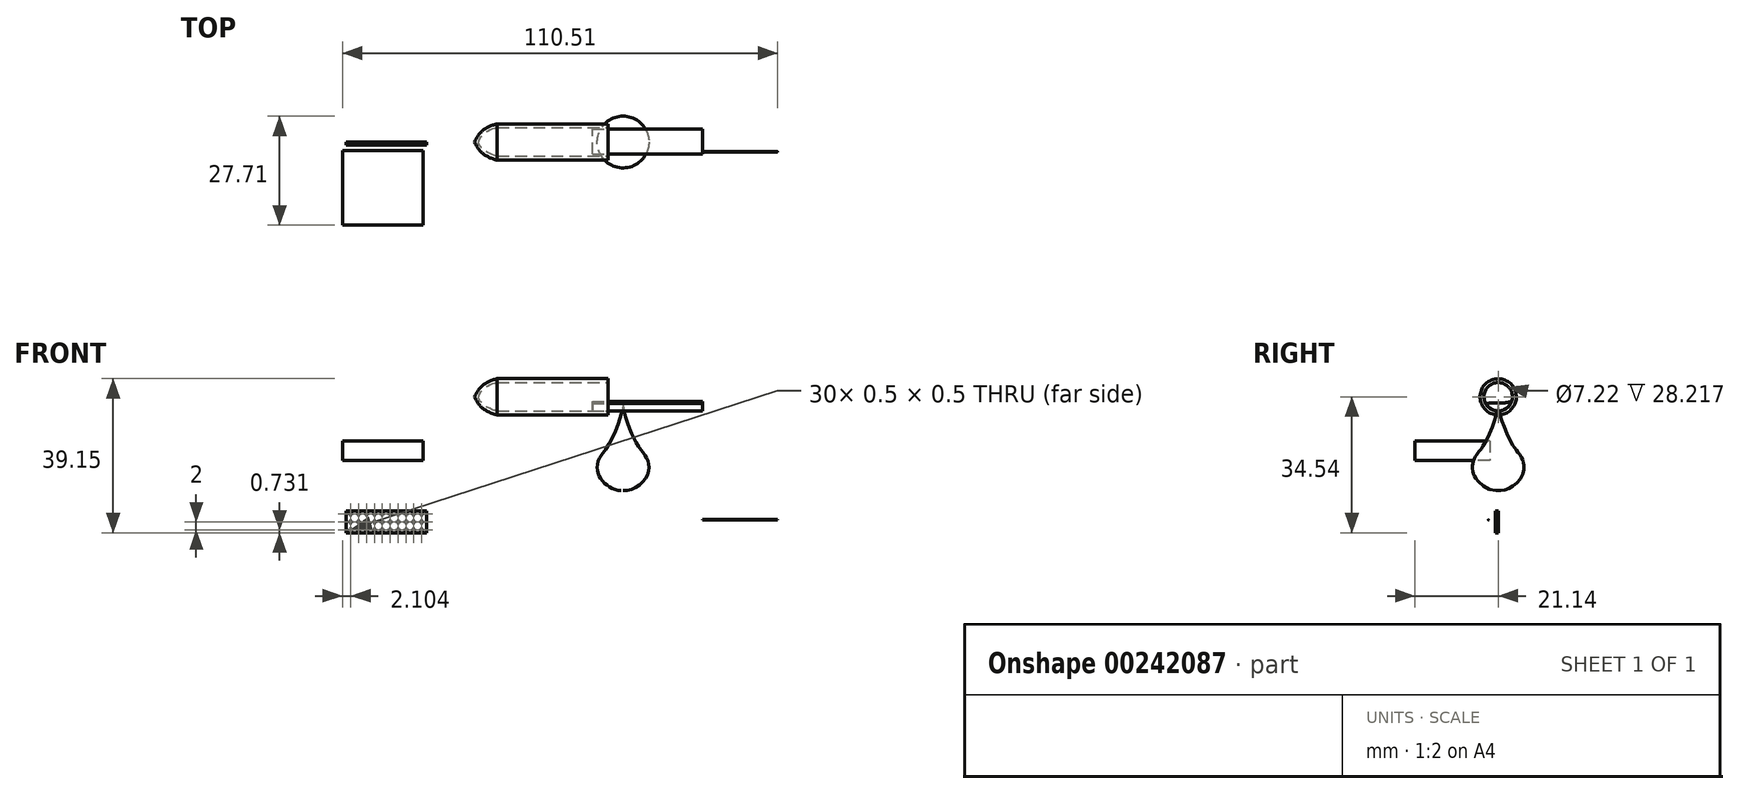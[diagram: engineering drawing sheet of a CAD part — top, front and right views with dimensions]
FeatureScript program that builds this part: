
annotation { "Feature Type Name" : "Feature", "Feature Type Description" : "" }
export const myFeature = defineFeature(function(context is Context, id is Id, definition is map)
    precondition{}
    {
        {
            var Q0;
            Q0=qCreatedBy(makeId("Front.planeOp"),FACE);
            var sketch = newSketch(context, id + "F0", { "sketchPlane" : qUnion([Q0])});
            skLineSegment(sketch, "E0.bottom", {"start": v(-89.66, -13.35) * mm, "end": v(-89.16, -13.35) * mm});
            skLineSegment(sketch, "E0.top", {"start": v(-89.66, -13.85) * mm, "end": v(-89.16, -13.85) * mm});
            skLineSegment(sketch, "E0.left", {"start": v(-89.66, -13.35) * mm, "end": v(-89.66, -13.85) * mm});
            skLineSegment(sketch, "E0.right", {"start": v(-89.16, -13.35) * mm, "end": v(-89.16, -13.85) * mm});
            skLineSegment(sketch, "E1.2.0.0", {"start": v(-87.66, -13.35) * mm, "end": v(-87.16, -13.35) * mm});
            skLineSegment(sketch, "E1.2.0.1", {"start": v(-87.16, -13.35) * mm, "end": v(-87.16, -13.85) * mm});
            skLineSegment(sketch, "E1.2.0.2", {"start": v(-87.66, -13.85) * mm, "end": v(-87.16, -13.85) * mm});
            skLineSegment(sketch, "E1.2.0.3", {"start": v(-87.66, -13.35) * mm, "end": v(-87.66, -13.85) * mm});
            skLineSegment(sketch, "E1.4.0.0", {"start": v(-85.66, -13.35) * mm, "end": v(-85.16, -13.35) * mm});
            skLineSegment(sketch, "E1.4.0.1", {"start": v(-85.16, -13.35) * mm, "end": v(-85.16, -13.85) * mm});
            skLineSegment(sketch, "E1.4.0.2", {"start": v(-85.66, -13.85) * mm, "end": v(-85.16, -13.85) * mm});
            skLineSegment(sketch, "E1.4.0.3", {"start": v(-85.66, -13.35) * mm, "end": v(-85.66, -13.85) * mm});
            skLineSegment(sketch, "E1.6.0.0", {"start": v(-83.66, -13.35) * mm, "end": v(-83.16, -13.35) * mm});
            skLineSegment(sketch, "E1.6.0.1", {"start": v(-83.16, -13.35) * mm, "end": v(-83.16, -13.85) * mm});
            skLineSegment(sketch, "E1.6.0.2", {"start": v(-83.66, -13.85) * mm, "end": v(-83.16, -13.85) * mm});
            skLineSegment(sketch, "E1.6.0.3", {"start": v(-83.66, -13.35) * mm, "end": v(-83.66, -13.85) * mm});
            skLineSegment(sketch, "E1.8.0.0", {"start": v(-81.66, -13.35) * mm, "end": v(-81.16, -13.35) * mm});
            skLineSegment(sketch, "E1.8.0.1", {"start": v(-81.16, -13.35) * mm, "end": v(-81.16, -13.85) * mm});
            skLineSegment(sketch, "E1.8.0.2", {"start": v(-81.66, -13.85) * mm, "end": v(-81.16, -13.85) * mm});
            skLineSegment(sketch, "E1.8.0.3", {"start": v(-81.66, -13.35) * mm, "end": v(-81.66, -13.85) * mm});
            skLineSegment(sketch, "E1.10.0.0", {"start": v(-79.66, -13.35) * mm, "end": v(-79.16, -13.35) * mm});
            skLineSegment(sketch, "E1.10.0.1", {"start": v(-79.16, -13.35) * mm, "end": v(-79.16, -13.85) * mm});
            skLineSegment(sketch, "E1.10.0.2", {"start": v(-79.66, -13.85) * mm, "end": v(-79.16, -13.85) * mm});
            skLineSegment(sketch, "E1.10.0.3", {"start": v(-79.66, -13.35) * mm, "end": v(-79.66, -13.85) * mm});
            skLineSegment(sketch, "E1.12.0.0", {"start": v(-77.66, -13.35) * mm, "end": v(-77.16, -13.35) * mm});
            skLineSegment(sketch, "E1.12.0.1", {"start": v(-77.16, -13.35) * mm, "end": v(-77.16, -13.85) * mm});
            skLineSegment(sketch, "E1.12.0.2", {"start": v(-77.66, -13.85) * mm, "end": v(-77.16, -13.85) * mm});
            skLineSegment(sketch, "E1.12.0.3", {"start": v(-77.66, -13.35) * mm, "end": v(-77.66, -13.85) * mm});
            skLineSegment(sketch, "E1.14.0.0", {"start": v(-75.66, -13.35) * mm, "end": v(-75.16, -13.35) * mm});
            skLineSegment(sketch, "E1.14.0.1", {"start": v(-75.16, -13.35) * mm, "end": v(-75.16, -13.85) * mm});
            skLineSegment(sketch, "E1.14.0.2", {"start": v(-75.66, -13.85) * mm, "end": v(-75.16, -13.85) * mm});
            skLineSegment(sketch, "E1.14.0.3", {"start": v(-75.66, -13.35) * mm, "end": v(-75.66, -13.85) * mm});
            skLineSegment(sketch, "E1.16.0.0", {"start": v(-73.66, -13.35) * mm, "end": v(-73.16, -13.35) * mm});
            skLineSegment(sketch, "E1.16.0.1", {"start": v(-73.16, -13.35) * mm, "end": v(-73.16, -13.85) * mm});
            skLineSegment(sketch, "E1.16.0.2", {"start": v(-73.66, -13.85) * mm, "end": v(-73.16, -13.85) * mm});
            skLineSegment(sketch, "E1.16.0.3", {"start": v(-73.66, -13.35) * mm, "end": v(-73.66, -13.85) * mm});
            skLineSegment(sketch, "E1.18.0.0", {"start": v(-71.66, -13.35) * mm, "end": v(-71.16, -13.35) * mm});
            skLineSegment(sketch, "E1.18.0.1", {"start": v(-71.16, -13.35) * mm, "end": v(-71.16, -13.85) * mm});
            skLineSegment(sketch, "E1.18.0.2", {"start": v(-71.66, -13.85) * mm, "end": v(-71.16, -13.85) * mm});
            skLineSegment(sketch, "E1.18.0.3", {"start": v(-71.66, -13.35) * mm, "end": v(-71.66, -13.85) * mm});
            skLineSegment(sketch, "E2.MirrorCS", {"start": v(-79.66, -15.87) * mm, "end": v(-79.16, -15.87) * mm});
            skLineSegment(sketch, "E3.MirrorCS", {"start": v(-89.16, -15.37) * mm, "end": v(-89.16, -15.87) * mm});
            skLineSegment(sketch, "E4.MirrorCS", {"start": v(-71.16, -15.37) * mm, "end": v(-71.16, -15.87) * mm});
            skLineSegment(sketch, "E5.MirrorCS", {"start": v(-77.66, -15.37) * mm, "end": v(-77.66, -15.87) * mm});
            skLineSegment(sketch, "E6.MirrorCS", {"start": v(-81.66, -15.37) * mm, "end": v(-81.66, -15.87) * mm});
            skLineSegment(sketch, "E7.MirrorCS", {"start": v(-75.66, -15.37) * mm, "end": v(-75.66, -15.87) * mm});
            skLineSegment(sketch, "E8.MirrorCS", {"start": v(-79.66, -15.37) * mm, "end": v(-79.66, -15.87) * mm});
            skLineSegment(sketch, "E9.MirrorCS", {"start": v(-83.66, -15.37) * mm, "end": v(-83.66, -15.87) * mm});
            skLineSegment(sketch, "E10.MirrorCS", {"start": v(-83.16, -15.37) * mm, "end": v(-83.16, -15.87) * mm});
            skLineSegment(sketch, "E11.MirrorCS", {"start": v(-77.16, -15.37) * mm, "end": v(-77.16, -15.87) * mm});
            skLineSegment(sketch, "E12.MirrorCS", {"start": v(-71.66, -15.37) * mm, "end": v(-71.16, -15.37) * mm});
            skLineSegment(sketch, "E13.MirrorCS", {"start": v(-87.66, -15.87) * mm, "end": v(-87.16, -15.87) * mm});
            skLineSegment(sketch, "E14.MirrorCS", {"start": v(-85.66, -15.37) * mm, "end": v(-85.66, -15.87) * mm});
            skLineSegment(sketch, "E15.MirrorCS", {"start": v(-85.66, -15.37) * mm, "end": v(-85.16, -15.37) * mm});
            skLineSegment(sketch, "E16.MirrorCS", {"start": v(-79.16, -15.37) * mm, "end": v(-79.16, -15.87) * mm});
            skLineSegment(sketch, "E17.MirrorCS", {"start": v(-71.66, -15.87) * mm, "end": v(-71.16, -15.87) * mm});
            skLineSegment(sketch, "E18.MirrorCS", {"start": v(-81.16, -15.37) * mm, "end": v(-81.16, -15.87) * mm});
            skLineSegment(sketch, "E19.MirrorCS", {"start": v(-81.66, -15.87) * mm, "end": v(-81.16, -15.87) * mm});
            skLineSegment(sketch, "E20.MirrorCS", {"start": v(-73.66, -15.37) * mm, "end": v(-73.66, -15.87) * mm});
            skLineSegment(sketch, "E21.MirrorCS", {"start": v(-85.16, -15.37) * mm, "end": v(-85.16, -15.87) * mm});
            skLineSegment(sketch, "E22.MirrorCS", {"start": v(-77.66, -15.87) * mm, "end": v(-77.16, -15.87) * mm});
            skLineSegment(sketch, "E23.MirrorCS", {"start": v(-87.66, -15.37) * mm, "end": v(-87.16, -15.37) * mm});
            skLineSegment(sketch, "E24.MirrorCS", {"start": v(-85.66, -15.87) * mm, "end": v(-85.16, -15.87) * mm});
            skLineSegment(sketch, "E25.MirrorCS", {"start": v(-77.66, -15.37) * mm, "end": v(-77.16, -15.37) * mm});
            skLineSegment(sketch, "E26.MirrorCS", {"start": v(-89.66, -15.87) * mm, "end": v(-89.16, -15.87) * mm});
            skLineSegment(sketch, "E27.MirrorCS", {"start": v(-87.16, -15.37) * mm, "end": v(-87.16, -15.87) * mm});
            skLineSegment(sketch, "E28.MirrorCS", {"start": v(-89.66, -15.37) * mm, "end": v(-89.16, -15.37) * mm});
            skLineSegment(sketch, "E29.MirrorCS", {"start": v(-83.66, -15.87) * mm, "end": v(-83.16, -15.87) * mm});
            skLineSegment(sketch, "E30.MirrorCS", {"start": v(-73.66, -15.87) * mm, "end": v(-73.16, -15.87) * mm});
            skLineSegment(sketch, "E31.MirrorCS", {"start": v(-73.66, -15.37) * mm, "end": v(-73.16, -15.37) * mm});
            skLineSegment(sketch, "E32.MirrorCS", {"start": v(-75.16, -15.37) * mm, "end": v(-75.16, -15.87) * mm});
            skLineSegment(sketch, "E33.MirrorCS", {"start": v(-71.66, -15.37) * mm, "end": v(-71.66, -15.87) * mm});
            skLineSegment(sketch, "E34.MirrorCS", {"start": v(-75.66, -15.37) * mm, "end": v(-75.16, -15.37) * mm});
            skLineSegment(sketch, "E35.MirrorCS", {"start": v(-89.66, -15.37) * mm, "end": v(-89.66, -15.87) * mm});
            skLineSegment(sketch, "E36.MirrorCS", {"start": v(-79.66, -15.37) * mm, "end": v(-79.16, -15.37) * mm});
            skLineSegment(sketch, "E37.MirrorCS", {"start": v(-87.66, -15.37) * mm, "end": v(-87.66, -15.87) * mm});
            skLineSegment(sketch, "E38.MirrorCS", {"start": v(-73.16, -15.37) * mm, "end": v(-73.16, -15.87) * mm});
            skLineSegment(sketch, "E39.MirrorCS", {"start": v(-75.66, -15.87) * mm, "end": v(-75.16, -15.87) * mm});
            skLineSegment(sketch, "E40.MirrorCS", {"start": v(-83.66, -15.37) * mm, "end": v(-83.16, -15.37) * mm});
            skLineSegment(sketch, "E41.MirrorCS", {"start": v(-81.66, -15.37) * mm, "end": v(-81.16, -15.37) * mm});
            skLineSegment(sketch, "E42.MirrorCS", {"start": v(-89.66, -17.37) * mm, "end": v(-89.16, -17.37) * mm});
            skLineSegment(sketch, "E43.MirrorCS", {"start": v(-79.66, -17.37) * mm, "end": v(-79.16, -17.37) * mm});
            skLineSegment(sketch, "E44.MirrorCS", {"start": v(-75.66, -17.37) * mm, "end": v(-75.16, -17.37) * mm});
            skLineSegment(sketch, "E45.MirrorCS", {"start": v(-87.66, -17.37) * mm, "end": v(-87.66, -17.87) * mm});
            skLineSegment(sketch, "E46.MirrorCS", {"start": v(-73.16, -17.37) * mm, "end": v(-73.16, -17.87) * mm});
            skLineSegment(sketch, "E47.MirrorCS", {"start": v(-83.66, -17.37) * mm, "end": v(-83.16, -17.37) * mm});
            skLineSegment(sketch, "E48.MirrorCS", {"start": v(-83.66, -17.87) * mm, "end": v(-83.16, -17.87) * mm});
            skLineSegment(sketch, "E49.MirrorCS", {"start": v(-81.66, -17.37) * mm, "end": v(-81.16, -17.37) * mm});
            skLineSegment(sketch, "E50.MirrorCS", {"start": v(-77.66, -17.37) * mm, "end": v(-77.16, -17.37) * mm});
            skLineSegment(sketch, "E51.MirrorCS", {"start": v(-85.66, -17.87) * mm, "end": v(-85.16, -17.87) * mm});
            skLineSegment(sketch, "E52.MirrorCS", {"start": v(-75.16, -17.37) * mm, "end": v(-75.16, -17.87) * mm});
            skLineSegment(sketch, "E53.MirrorCS", {"start": v(-75.66, -17.87) * mm, "end": v(-75.16, -17.87) * mm});
            skLineSegment(sketch, "E54.MirrorCS", {"start": v(-89.66, -17.37) * mm, "end": v(-89.66, -17.87) * mm});
            skLineSegment(sketch, "E55.MirrorCS", {"start": v(-89.66, -17.87) * mm, "end": v(-89.16, -17.87) * mm});
            skLineSegment(sketch, "E56.MirrorCS", {"start": v(-71.66, -17.37) * mm, "end": v(-71.66, -17.87) * mm});
            skLineSegment(sketch, "E57.MirrorCS", {"start": v(-87.16, -17.37) * mm, "end": v(-87.16, -17.87) * mm});
            skLineSegment(sketch, "E58.MirrorCS", {"start": v(-73.66, -17.87) * mm, "end": v(-73.16, -17.87) * mm});
            skLineSegment(sketch, "E59.MirrorCS", {"start": v(-73.66, -17.37) * mm, "end": v(-73.16, -17.37) * mm});
            skLineSegment(sketch, "E60.MirrorCS", {"start": v(-71.16, -17.37) * mm, "end": v(-71.16, -17.87) * mm});
            skLineSegment(sketch, "E61.MirrorCS", {"start": v(-77.66, -17.37) * mm, "end": v(-77.66, -17.87) * mm});
            skLineSegment(sketch, "E62.MirrorCS", {"start": v(-89.16, -17.37) * mm, "end": v(-89.16, -17.87) * mm});
            skLineSegment(sketch, "E63.MirrorCS", {"start": v(-79.66, -17.87) * mm, "end": v(-79.16, -17.87) * mm});
            skLineSegment(sketch, "E64.MirrorCS", {"start": v(-87.66, -17.37) * mm, "end": v(-87.16, -17.37) * mm});
            skLineSegment(sketch, "E65.MirrorCS", {"start": v(-77.66, -17.87) * mm, "end": v(-77.16, -17.87) * mm});
            skLineSegment(sketch, "E66.MirrorCS", {"start": v(-85.16, -17.37) * mm, "end": v(-85.16, -17.87) * mm});
            skLineSegment(sketch, "E67.MirrorCS", {"start": v(-73.66, -17.37) * mm, "end": v(-73.66, -17.87) * mm});
            skLineSegment(sketch, "E68.MirrorCS", {"start": v(-81.66, -17.87) * mm, "end": v(-81.16, -17.87) * mm});
            skLineSegment(sketch, "E69.MirrorCS", {"start": v(-81.16, -17.37) * mm, "end": v(-81.16, -17.87) * mm});
            skLineSegment(sketch, "E70.MirrorCS", {"start": v(-71.66, -17.87) * mm, "end": v(-71.16, -17.87) * mm});
            skLineSegment(sketch, "E71.MirrorCS", {"start": v(-79.16, -17.37) * mm, "end": v(-79.16, -17.87) * mm});
            skLineSegment(sketch, "E72.MirrorCS", {"start": v(-79.66, -17.37) * mm, "end": v(-79.66, -17.87) * mm});
            skLineSegment(sketch, "E73.MirrorCS", {"start": v(-75.66, -17.37) * mm, "end": v(-75.66, -17.87) * mm});
            skLineSegment(sketch, "E74.MirrorCS", {"start": v(-85.66, -17.37) * mm, "end": v(-85.16, -17.37) * mm});
            skLineSegment(sketch, "E75.MirrorCS", {"start": v(-77.16, -17.37) * mm, "end": v(-77.16, -17.87) * mm});
            skLineSegment(sketch, "E76.MirrorCS", {"start": v(-87.66, -17.87) * mm, "end": v(-87.16, -17.87) * mm});
            skLineSegment(sketch, "E77.MirrorCS", {"start": v(-85.66, -17.37) * mm, "end": v(-85.66, -17.87) * mm});
            skLineSegment(sketch, "E78.MirrorCS", {"start": v(-83.66, -17.37) * mm, "end": v(-83.66, -17.87) * mm});
            skLineSegment(sketch, "E79.MirrorCS", {"start": v(-71.66, -17.37) * mm, "end": v(-71.16, -17.37) * mm});
            skLineSegment(sketch, "E80.MirrorCS", {"start": v(-81.66, -17.37) * mm, "end": v(-81.66, -17.87) * mm});
            skLineSegment(sketch, "E81.MirrorCS", {"start": v(-83.16, -17.37) * mm, "end": v(-83.16, -17.87) * mm});
            skLineSegment(sketch, "E82.bottom", {"start": v(-90.66, -12.85) * mm, "end": v(-70.16, -12.85) * mm});
            skLineSegment(sketch, "E82.top", {"start": v(-90.66, -18.35) * mm, "end": v(-70.16, -18.35) * mm});
            skLineSegment(sketch, "E82.left", {"start": v(-90.66, -12.85) * mm, "end": v(-90.66, -18.35) * mm});
            skLineSegment(sketch, "E82.right", {"start": v(-70.16, -12.85) * mm, "end": v(-70.16, -18.35) * mm});
            skSolve(sketch);
        }
        {
            var Q0;
            Q0=makeQuery(id+"F0.imprint","IMPRINT",FACE,{"disambiguationData":[TD([[makeQuery(id+"F0.imprint","IMPRINT",EDGE,{"derivedFrom":sQuery(id+"F0.wireOp",EDGE,"E0.bottom")}),1.0]])]});
            extrude(context, id + "F1", {"entities" : qUnion([Q0]), "depth" : 0.75 * mm});
        }
        {
            var Q0;
            Q0=qCreatedBy(makeId("Right.planeOp"),FACE);
            var sketch = newSketch(context, id + "F2", { "sketchPlane" : qUnion([Q0])});
            skCircle(sketch, "E83", {"center": v(-2.48, -15.07) * mm, "radius": 0.05 * mm});
            skSolve(sketch);
        }
        {
            var Q0;
            Q0=makeQuery(id+"F2.imprint","IMPRINT",FACE,{"disambiguationData":[TD([[makeQuery(id+"F2.imprint","IMPRINT",EDGE,{"derivedFrom":sQuery(id+"F2.wireOp",EDGE,"E83")}),1.0]])]});
            extrude(context, id + "F3", {"entities" : qUnion([Q0]), "depth" : 19 * mm});
        }
        {
            var Q0;
            Q0=qCreatedBy(makeId("Top.planeOp"),FACE);
            var sketch = newSketch(context, id + "F4", { "sketchPlane" : qUnion([Q0])});
            skLineSegment(sketch, "E84.bottom", {"start": v(-91.5, -2.14) * mm, "end": v(-71, -2.14) * mm});
            skLineSegment(sketch, "E84.top", {"start": v(-91.5, -21.14) * mm, "end": v(-71, -21.14) * mm});
            skLineSegment(sketch, "E84.left", {"start": v(-91.5, -2.14) * mm, "end": v(-91.5, -21.14) * mm});
            skLineSegment(sketch, "E84.right", {"start": v(-71, -2.14) * mm, "end": v(-71, -21.14) * mm});
            skSolve(sketch);
        }
        {
            var Q0;
            Q0=makeQuery(id+"F4.imprint","IMPRINT",FACE,{"disambiguationData":[TD([[makeQuery(id+"F4.imprint","IMPRINT",EDGE,{"derivedFrom":sQuery(id+"F4.wireOp",EDGE,"E84.bottom")}),-1.0]])]});
            extrude(context, id + "F5", {"entities" : qUnion([Q0]), "depth" : 5 * mm});
        }
        {
            var Q0;
            Q0=qCreatedBy(makeId("Front.planeOp"),FACE);
            var sketch = newSketch(context, id + "F6", { "sketchPlane" : qUnion([Q0])});
            skLineSegment(sketch, "E85", {"start": v(-20.23, 14.01) * mm, "end": v(-20.23, -7.6) * mm});
            skFitSpline(sketch, "E86", {"points": [v(-20.23, 14.01) * mm, v(-16.26, 3.54) * mm, v(-13.95, 0) * mm, v(-14.5, -4.5) * mm, v(-20.23, -7.6) * mm], "startDerivative": vector(6.72, -37.8) * mm, "endDerivative": vector(-23.74, 4.03) * mm});
            skSolve(sketch);
        }
        {
            var Q0;
            Q0=makeQuery(id+"F6.imprint","IMPRINT",FACE,{"disambiguationData":[TD([[makeQuery(id+"F6.imprint","IMPRINT",EDGE,{"derivedFrom":sQuery(id+"F6.wireOp",EDGE,"E85")}),1.0]])]});
            var Q1;
            Q1=sQuery(id+"F6.wireOp",EDGE,"E85");
            revolve(context, id + "F7", {"entities" : qUnion([Q0]), "axis" : qUnion([Q1]), "revolveType" : RevolveType.FULL});
        }
        {
            var Q0;
            Q0=qCreatedBy(makeId("Front.planeOp"),FACE);
            var sketch = newSketch(context, id + "F8", { "sketchPlane" : qUnion([Q0])});
            skLineSegment(sketch, "E87", {"start": v(-24.02, 16.19) * mm, "end": v(-57.94, 16.19) * mm, "construction": true});
            skLineSegment(sketch, "E88", {"start": v(-24.02, 11.58) * mm, "end": v(-52.23, 11.58) * mm});
            skFitSpline(sketch, "E89", {"points": [v(-52.23, 11.58) * mm, v(-57.94, 16.19) * mm], "startDerivative": vector(-10.67, 2.67) * mm, "endDerivative": vector(-2.33, 5.67) * mm});
            skLineSegment(sketch, "E90", {"start": v(-24.02, 11.58) * mm, "end": v(-24.02, 12.58) * mm});
            skLineSegment(sketch, "E91", {"start": v(-24.02, 12.58) * mm, "end": v(-52.23, 12.58) * mm});
            skFitSpline(sketch, "E92", {"points": [v(-52.23, 12.58) * mm, v(-57, 16.19) * mm], "startDerivative": vector(-9.03, 1.99) * mm, "endDerivative": vector(-0.19, 3.01) * mm});
            skLineSegment(sketch, "E93", {"start": v(-57, 16.19) * mm, "end": v(-57.94, 16.19) * mm});
            skSolve(sketch);
        }
        {
            var Q0;
            Q0 = qSketchRegion(id + "F8", true);
            var Q1;
            Q1=sQuery(id+"F8.wireOp",EDGE,"E87");
            revolve(context, id + "F9", {"entities" : qUnion([Q0]), "axis" : qUnion([Q1]), "revolveType" : RevolveType.FULL});
        }
        {
            var Q0;
            Q0=qCreatedBy(makeId("Right.planeOp"),FACE);
            var sketch = newSketch(context, id + "F10", { "sketchPlane" : qUnion([Q0])});
            skCircle(sketch, "E94", {"center": v(0, 16.15) * mm, "radius": 3.54 * mm, "construction": true});
            skArc(sketch, "E95", {"start": v(3.33, 14.96) * mm, "mid": v(0.26, 12.62) * mm, "end": v(-3.12, 14.48) * mm});
            skFitSpline(sketch, "E96", {"points": [v(-3.12, 14.48) * mm, v(3.33, 14.96) * mm], "startDerivative": vector(6.62, 1.25) * mm, "endDerivative": vector(6.6, 1.81) * mm});
            skSolve(sketch);
        }
        {
            var Q0;
            Q0 = qSketchRegion(id + "F10", true);
            extrude(context, id + "F11", {"entities" : qUnion([Q0]), "oppositeDirection" : true, "depth" : 28 * mm});
        }
    });
